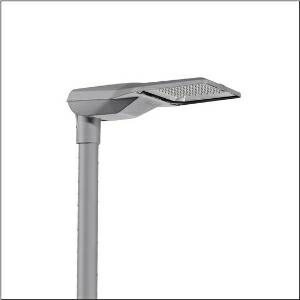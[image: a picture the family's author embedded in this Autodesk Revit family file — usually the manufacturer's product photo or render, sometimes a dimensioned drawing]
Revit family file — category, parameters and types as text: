
# Revit family: streetlight_sl_21_iq_midi___pc-r_5xe3g31g08mb_83c1
name_source: partatom
category: Lighting Fixtures
units: mm (PartAtom-declared; Revit-internal decimal feet)

## family parameters
Cut with Voids When Loaded = No
Host = Face
Light Source = No
Part Type = Normal
Room Calculation Point = No
Round Connector Dimension = Use Diameter
Shared = No

## types (1)
- --- (1 x LED, 18560 lm, 146.7 W, 3000K)
    Apparent Load = 147 VA
    CIE Flux Codes = 38 78 98 100 100
    Color Rendering = 70
    Color Temperature = 3000K
    Default Elevation = 1800 mm
    Description = Streetlight SL 21 iQ midi, mast luminaire, primary light control with lens, of PMMA, primary optical cover: cover, of toughened safety glass, transparent, light distribution: PC-R, light emission: direct distribution, primary light characteristic: asymmetric, right, installation type: post-top, side-entry, LED, High Power LED, rated luminous flux: 18.560lm, luminous efficacy: 127lm/W, light colour: 730, colour temperature: 3000K, control gear: iQ Street-Remote, control: Street-Remote, Auto-Match, Temp-Guard, Lumen-Switch, Night-Set, Smart-Wire, Light-Fading, Desk-Remote (wireless, voltage-free reading and setting of iQ features in the workshop via application-optimized NFC function/RFID function), optimised constant luminous flux control (CLO 2.0), pre-setting: linear dimming characteristic, mains connection: 230..240V, AC, 50/60Hz, start of lifetime: 147W, end of service life: 161W, reduction: 62W, luminaire housing, of diecast aluminium, powder-coated, Siteco® metallic grey (DB 702S), corrosivity category C5 mid according to DIN EN ISO 12944, please order mast flange separately, inclination adjustable: 0°, 5°, 10°, 15°, sealing non-destructively replaceable, multi-level sealing system, length: 644mm, width: 335mm, height: 110mm, mast flange for spigot size: 42mm (side-entry): 5XC10008XM4, 60/48mm (side-entry/post-top): 5XC10108XM2, 76/60mm (side-entry/post-top): 5XC10108XM1, mounting height: 4..8m, protection rating (complete): IP66, insulation class (complete): insulation class II (safety insulation), certification: CE, ENEC, ENEC+, VDE, impact resistance: IK10, permissible operating ambient temperature for outdoor applications: -40..+50°C, standard-compliant lighting for roads and squares, packaging unit: 1 piece

Light Distribution: PC-R
    Height = 111 mm
    Lamp = 1 x LED
    Lamp Light Flux = 18560 lm
    Lamp Power = 146.7 W
    Lamp count = 1
    Length = 644 mm
    Luminous efficacy = 127 lm/W
    Manufacturer = Siteco
    ModVariant = No
    Model = 5XE3G31G08MB
    Number of Poles = 1
    OnlyDefault = Yes
    Power Factor = 1
    Product Name = Streetlight SL 21 iQ midi | PC-R
    Product group = mast luminaire | pylon top
    ProductGroupID = 6100
    Protection Class = Protection class II
    Protection Degree = IP 66
    RLX_Detail_Level = 1
    RLX_Emergency_Light_Flux = 0 lm
    RLX_Emergency_Type = 0
    RLX_Emergency_Type_DB = No
    RlxData = <blob elided: 29401 chars, md5=9f5aa738>
    Socket = socket
    Standby Power = 0 W
    System Light Flux = 18560 lm
    System Power = 147 W
    Type Comments = factory setting: luminous flux: 100 % | dim-lin: 254 | 753 mA
    Type Image = l_1004298.jpg
    URL = http://relux.com
    VarID = @adj_085459
    Voltage = 0 V
    Weight = 0.00 kg
    Width = 336 mm

## geometry (parser evidence)
native form markers: Blend x4, Sweep x9
no freeform markers — native parametric forms only
